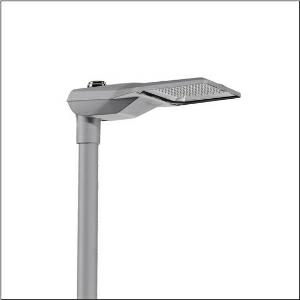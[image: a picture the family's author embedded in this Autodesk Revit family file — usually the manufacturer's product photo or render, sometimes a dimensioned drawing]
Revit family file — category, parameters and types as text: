
# Revit family: streetlight_sl_21_midi___p1_0a_5xe7a47n08mb_40bb
name_source: partatom
category: Lighting Fixtures
units: mm (PartAtom-declared; Revit-internal decimal feet)

## family parameters
Cut with Voids When Loaded = No
Host = Face
Light Source = No
Part Type = Normal
Room Calculation Point = No
Round Connector Dimension = Use Diameter
Shared = No

## types (1)
- --- (1 x LED, 20180 lm, 147 W, 4000K)
    Apparent Load = 147 VA
    CIE Flux Codes = 21 50 90 100 100
    Color Rendering = 70
    Color Temperature = 4000K
    Default Elevation = 1800 mm
    Description = Streetlight SL 21 midi, mast luminaire, primary light control with lens, of PMMA, primary optical cover: cover, of toughened safety glass, transparent, light distribution: P1.0a, light emission: direct distribution, primary light characteristic: asymmetric, installation type: side-entry, LED, 3G 2.5mm², High Power LED, rated luminous flux: 20.180lm, luminous efficacy: 137lm/W, light colour: 740, colour temperature: 4000K, control gear: NEMA (7pin), control: overheat protection, pre-setting: linear dimming characteristic, constant luminous flux control, time-dependent luminous flux control, flexible luminous flux parameterisation, mains connection: 220..240V, AC, 50/60Hz, connection cable pre-assembled, cable length: 12,5m, wiring characteristics: H05VV-F, start of lifetime: 147W, end of service life: 155W, reduction: 65W, luminaire housing, of diecast aluminium (EN AC-44300), powder-coated, SITECO metallic grey (DB 702S), corrosivity category C5 high according to DIN EN ISO 12944, multi-level sealing system, sealing non-destructively replaceable, inclination adjustable: 0°, 5°, 10°, 15°, length: 644mm, width: 335mm, height: 110mm, spigot size: 42mm (side-entry), mounting height: 4..8m, protection rating (complete): IP66, insulation class (complete): insulation class I (protective earthing), certification: CE, ENEC, ENEC+, VDE, impact resistance: IK10, permissible operating ambient temperature for outdoor applications: -40..+50°C, standard-compliant lighting for roads and squares, packaging unit: 1 piece

Light Distribution: P1.0a
    Height = 111 mm
    Lamp = 1 x LED
    Lamp Light Flux = 20180 lm
    Lamp Power = 147 W
    Lamp count = 1
    Length = 644 mm
    Luminous efficacy = 137 lm/W
    Manufacturer = Siteco
    ModVariant = No
    Model = 5XE7A47N08MB
    Number of Poles = 1
    OnlyDefault = Yes
    Power Factor = 1
    Product Name = Streetlight SL 21 midi | P1.0a
    Product group = mast luminaire | pylon top
    ProductGroupID = 6100
    Protection Class = Protection class I
    Protection Degree = IP 66
    RLX_Detail_Level = 1
    RLX_Emergency_Light_Flux = 0 lm
    RLX_Emergency_Type = 0
    RLX_Emergency_Type_DB = No
    RlxData = <blob elided: 37881 chars, md5=369c85c7>
    Socket = socket
    Standby Power = 0 W
    System Light Flux = 20180 lm
    System Power = 147 W
    Type Comments = factory setting: luminous flux: 100 % | dim-lin: 254 | 750 mA
    Type Image = l_1294377.jpg
    URL = http://relux.com
    VarID = @adj_133939
    Voltage = 0 V
    Weight = 0.00 kg
    Width = 336 mm

## geometry (parser evidence)
native form markers: Blend x4, Sweep x11
no freeform markers — native parametric forms only
